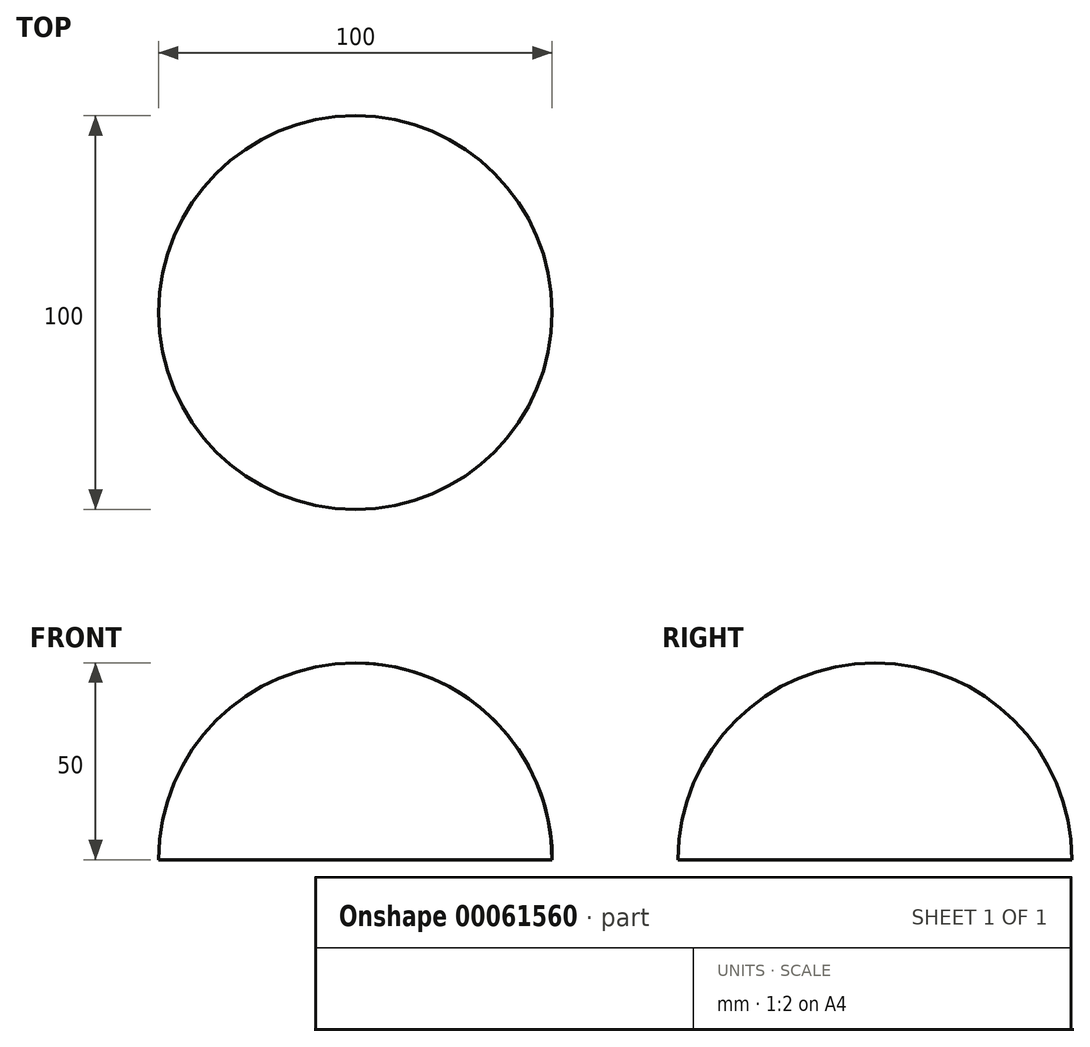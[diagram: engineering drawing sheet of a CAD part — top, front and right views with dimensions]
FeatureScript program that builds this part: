
annotation { "Feature Type Name" : "Feature", "Feature Type Description" : "" }
export const myFeature = defineFeature(function(context is Context, id is Id, definition is map)
    precondition{}
    {
        {
            var Q0;
            Q0=qCreatedBy(makeId("Front.planeOp"),FACE);
            var sketch = newSketch(context, id + "F0", { "sketchPlane" : qUnion([Q0])});
            skArc(sketch, "E0", {"start": v(50, 0) * mm, "mid": v(35.36, 35.36) * mm, "end": v(0, 50) * mm});
            skLineSegment(sketch, "E1", {"start": v(0, 0) * mm, "end": v(0, 50) * mm});
            skLineSegment(sketch, "E2", {"start": v(0, 0) * mm, "end": v(50, 0) * mm});
            skSolve(sketch);
        }
        {
            var Q0;
            Q0=makeQuery(id+"F0.imprint","IMPRINT",FACE,{"disambiguationData":[TD([[makeQuery(id+"F0.imprint","IMPRINT",EDGE,{"derivedFrom":sQuery(id+"F0.wireOp",EDGE,"E0")}),1.0]])]});
            var Q1;
            Q1=sQuery(id+"F0.wireOp",EDGE,"E1");
            revolve(context, id + "F1", {"surfaceOperationType" : NewSurfaceOperationType.NEW, "entities" : qUnion([Q0]), "axis" : qUnion([Q1]), "revolveType" : RevolveType.FULL});
        }
    });
